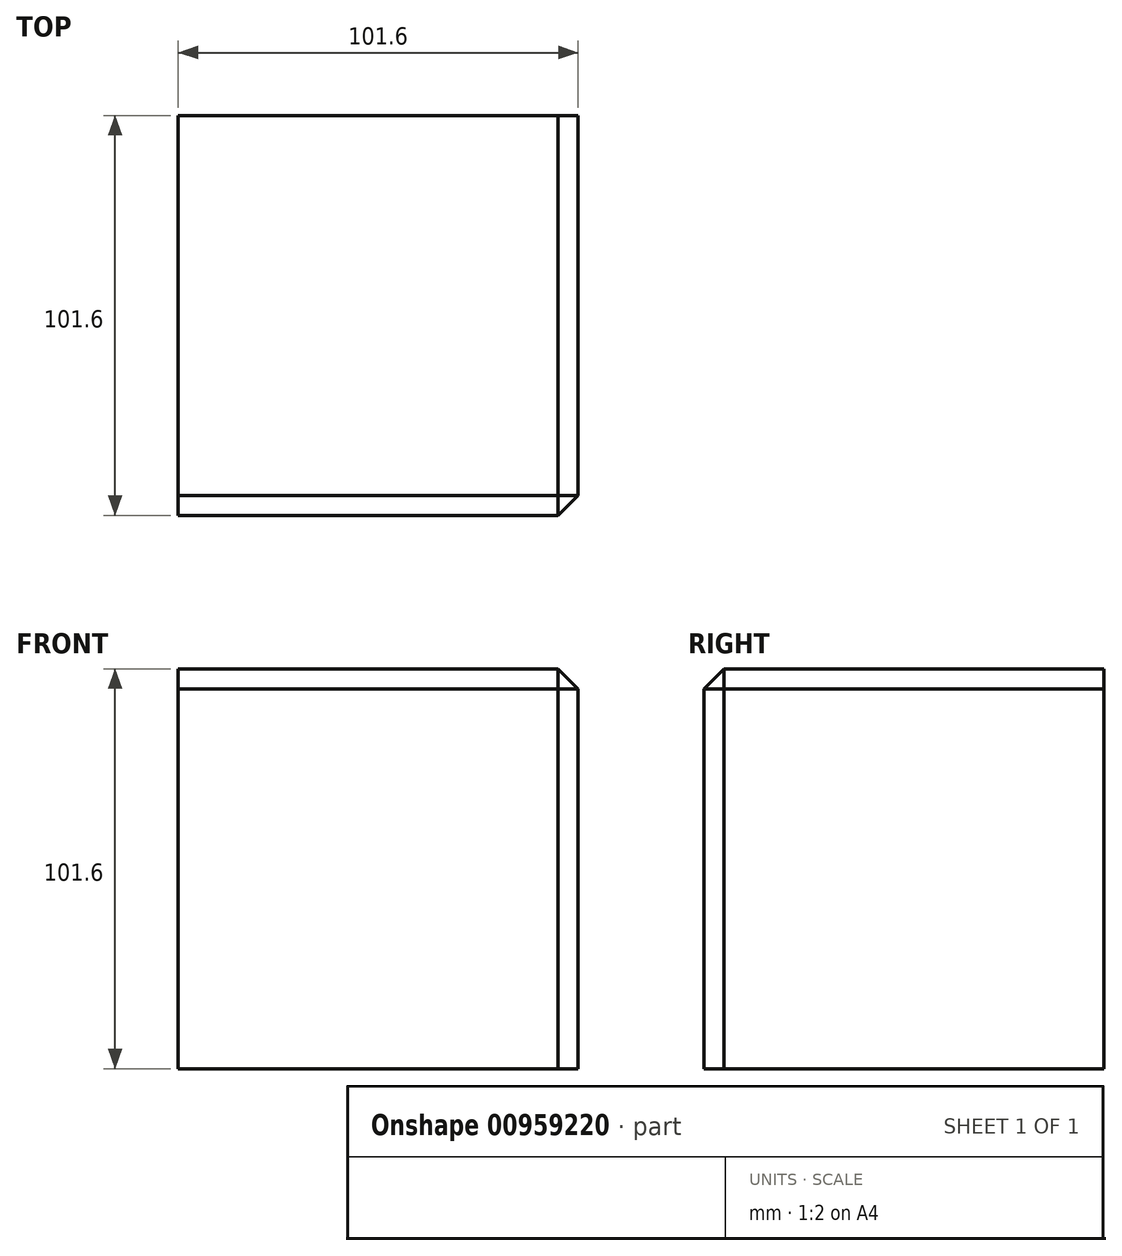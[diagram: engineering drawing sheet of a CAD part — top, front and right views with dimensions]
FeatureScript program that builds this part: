
annotation { "Feature Type Name" : "Feature", "Feature Type Description" : "" }
export const myFeature = defineFeature(function(context is Context, id is Id, definition is map)
    precondition{}
    {
        {
            var Q0;
            Q0=qCreatedBy(makeId("Front.planeOp"),FACE);
            var sketch = newSketch(context, id + "F0", { "sketchPlane" : qUnion([Q0])});
            skLineSegment(sketch, "E0.bottom", {"start": v(50.8, 50.8) * mm, "end": v(-50.8, 50.8) * mm});
            skLineSegment(sketch, "E0.top", {"start": v(50.8, -50.8) * mm, "end": v(-50.8, -50.8) * mm});
            skLineSegment(sketch, "E0.left", {"start": v(50.8, 50.8) * mm, "end": v(50.8, -50.8) * mm});
            skLineSegment(sketch, "E0.right", {"start": v(-50.8, 50.8) * mm, "end": v(-50.8, -50.8) * mm});
            skPoint(sketch, "E0.middle", {"position": v(0, 0) * mm});
            skSolve(sketch);
        }
        {
            var Q0;
            Q0=makeQuery(id+"F0.imprint","IMPRINT",FACE,{"disambiguationData":[TD([[makeQuery(id+"F0.imprint","IMPRINT",EDGE,{"derivedFrom":sQuery(id+"F0.wireOp",EDGE,"E0.bottom")}),1.0]])]});
            extrude(context, id + "F1", {"entities" : qUnion([Q0]), "depth" : 101.6 * mm, "offsetDistance" : 25.4 * mm});
        }
        {
            var Q0;
            Q0=makeQuery(id+"F1.opExtrude","SWEPT_EDGE",EDGE,{"disambiguationData":[OSD([sQuery(id+"F0.wireOp",EDGE,"E0.bottom"),sQuery(id+"F0.wireOp",EDGE,"E0.left")])]});
            var Q1;
            Q1=makeQuery(id+"F1.opExtrude","CAP_EDGE",EDGE,{"disambiguationData":[OSD([sQuery(id+"F0.wireOp",EDGE,"E0.bottom")])],"isStart":false});
            var Q2;
            Q2=makeQuery(id+"F1.opExtrude","CAP_EDGE",EDGE,{"disambiguationData":[OSD([sQuery(id+"F0.wireOp",EDGE,"E0.left")])],"isStart":false});
            chamfer(context, id + "F2", {"entities" : qUnion([Q0, Q1, Q2]), "width" : 5.08 * mm, "tangentPropagation" : true});
        }
    });
